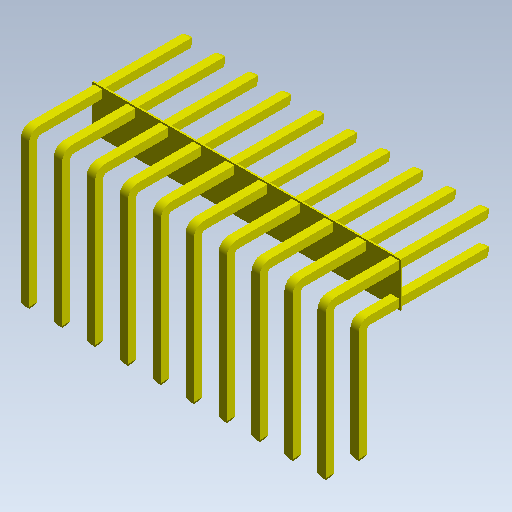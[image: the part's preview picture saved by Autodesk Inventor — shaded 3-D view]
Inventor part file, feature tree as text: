
AUTODESK INVENTOR PART (.ipt)
format: ipt  version: 2021 (Build 250183000, 183)  size: 501,248 bytes
history: native  units: mm (DEFAULTED — no unit token found)
features: extrude x7, sketch x7, other x7
ambient origin geometry x8: Origin, YZ Plane, XZ Plane, XY Plane, X Axis, Y Axis, Z Axis, Center Point
bodies: Solid1 (feature_tree)
feature tree (21):
  extrude  "Extrusion1"  Depth=23.749mm TaperAngle=0.0deg
  sketch  "Sketch_36"
  extrude  "Extrusion2"  Depth=10.16mm TaperAngle=0.0deg
  extrude  "Extrusion3"  Depth=10.16mm TaperAngle=0.0deg
  extrude  "Extrusion4"  [1 undecoded]
  extrude  "Extrusion5"  [1 undecoded]
  extrude  "Extrusion6"  [1 undecoded]
  extrude  "Extrusion7"  [1 undecoded]
  other  "pin_XY"
  other  "pin_YZ"
  other  "pin_ZX"
  other  "pin_X"
  other  "pin_Y"
  other  "pin_Z"
  other  "pin_Center"
  sketch  "Sketch_1"  dims[d0=23.495mm d1=0.0mm d2=23.749mm d3=0.0mm]
  sketch  "Sketch_26"  dims[d12=20.32mm d13=0.0mm]
  sketch  "Sketch_9"  dims[d4=23.495mm d5=0.0mm d6=10.16mm d7=0.0mm]
  sketch  "Sketch_12"  dims[d8=508.0mm d9=0.0mm d10=10.16mm d11=0.0mm]
  sketch  "Sketch_33"
  sketch  "Sketch_38"
note: 4 required parameter values undecoded (feature->parameter linkage not recoverable at this tier; creation-order binding heuristic only, values carry confidence <= 0.55)
